# Revit family: Seating-Stacking_Stool-Teknion-Zones_ZNMS_Low_Backless-R2013
name_source: partatom
category: Furniture
revit_build: Autodesk Revit Architecture 2013 (Build: 20130531_2115(x64)
units: mm (PartAtom-declared; Revit-internal decimal feet)

## types (2) — shared parameters
Assembly Code = E2020200
Depth = 16 19/32"
Height = 17 31/32"
Manufacturer = Teknion
Manufacturer Fax = 416.661.4586
Product Documentation Link = http://www.teknion.com
Product Line = Zones
Product Page URL = http://www.teknion.com
Series = Zones
Sustainability Data = http://www.teknion.com
URL = www.teknion.com
Warranty = http://www.teknion.com
Width = 16 19/32"

## per-type parameters (varying)
| type | Description | Model | Part Number | With Seat Upholstery Finish | With Seat Wood Frame Finish |
| Stacking Low Backless Stool, Wood | Zones Stacking Low Backless Stool, 4-Wood Legs + Seat | ZNMSW | ZNMSW | No | Yes |
| Stacking Low Backless Stool, Upholstered | Zones Stacking Low Backless Stool, 4-Wood Legs, Uph. | ZNMSU | ZNMSU | Yes | No |

## geometry (parser evidence)
native form markers: Blend x55, Sweep x1
no freeform markers — native parametric forms only
